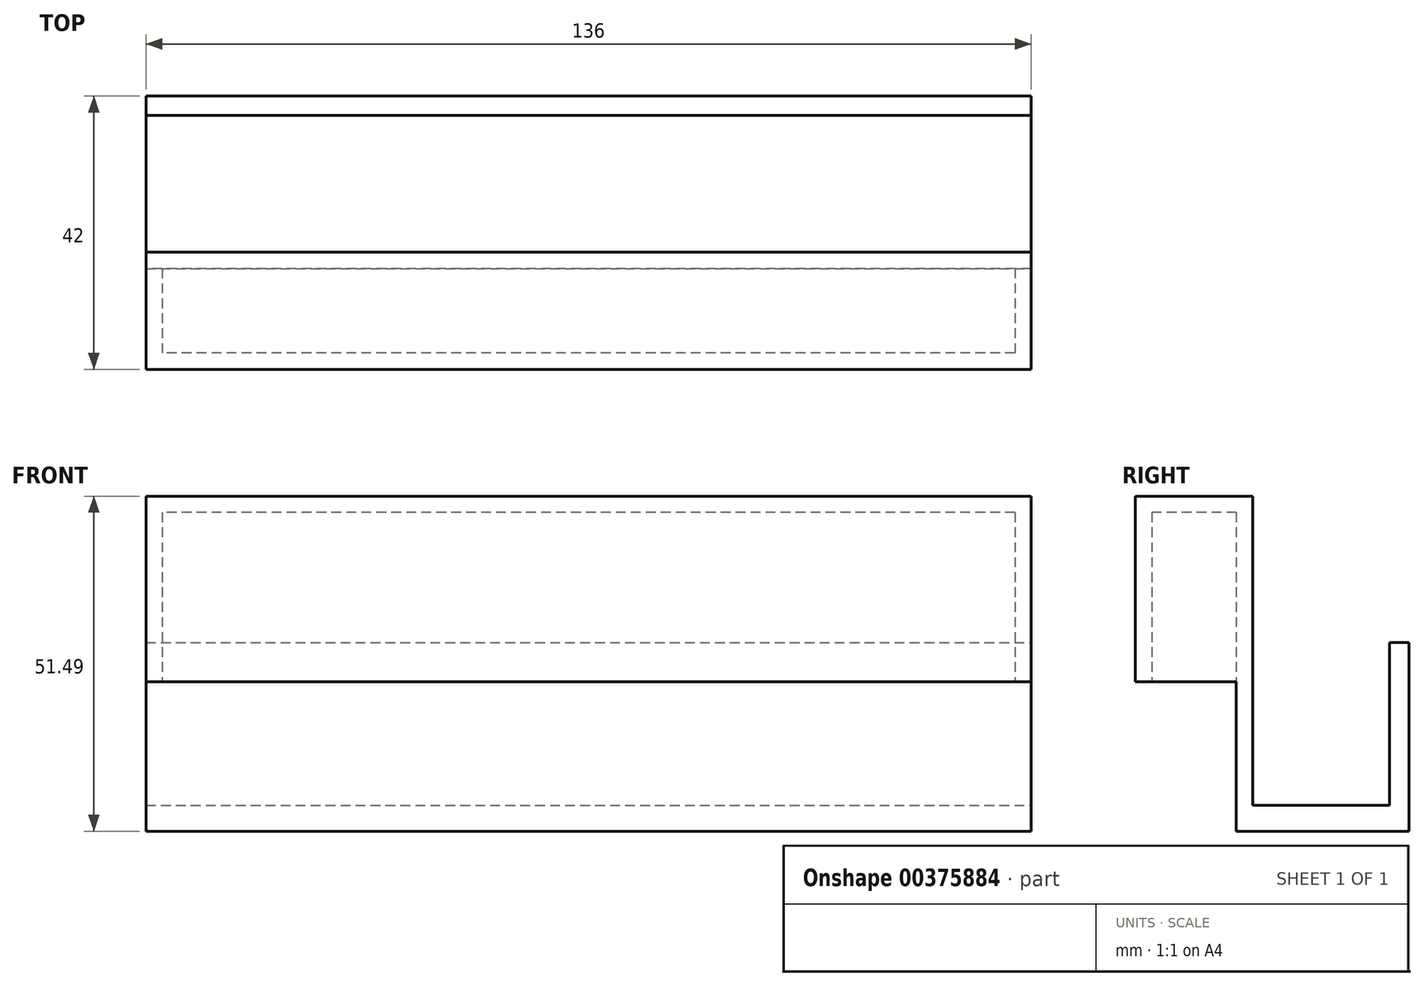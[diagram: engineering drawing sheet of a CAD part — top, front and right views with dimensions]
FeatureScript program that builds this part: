
annotation { "Feature Type Name" : "Feature", "Feature Type Description" : "" }
export const myFeature = defineFeature(function(context is Context, id is Id, definition is map)
    precondition{}
    {
        {
            var Q0;
            Q0=qCreatedBy(makeId("Top.planeOp"),FACE);
            var sketch = newSketch(context, id + "F0", { "sketchPlane" : qUnion([Q0])});
            skLineSegment(sketch, "E0.bottom", {"start": v(65.5, 6.5) * mm, "end": v(-65.5, 6.5) * mm});
            skLineSegment(sketch, "E0.top", {"start": v(65.5, -6.5) * mm, "end": v(-65.5, -6.5) * mm});
            skLineSegment(sketch, "E0.left", {"start": v(65.5, 6.5) * mm, "end": v(65.5, -6.5) * mm});
            skLineSegment(sketch, "E0.right", {"start": v(-65.5, 6.5) * mm, "end": v(-65.5, -6.5) * mm});
            skPoint(sketch, "E0.middle", {"position": v(0, 0) * mm});
            skSolve(sketch);
        }
        {
            var Q0;
            Q0=makeQuery(id+"F0.imprint","IMPRINT",FACE,{"disambiguationData":[TD([[makeQuery(id+"F0.imprint","IMPRINT",EDGE,{"derivedFrom":sQuery(id+"F0.wireOp",EDGE,"E0.bottom")}),1.0]])]});
            extrude(context, id + "F1", {"entities" : qUnion([Q0]), "depth" : 26 * mm});
        }
        {
            var Q0;
            Q0=makeQuery(id+"F1.opExtrude","CAP_FACE",FACE,{"disambiguationData":[OSD([sQuery(id+"F0.wireOp",EDGE,"E0.bottom"),sQuery(id+"F0.wireOp",EDGE,"E0.top"),sQuery(id+"F0.wireOp",EDGE,"E0.left"),sQuery(id+"F0.wireOp",EDGE,"E0.right")])],"isStart":true});
            shell(context, id + "F2", {"entities" : qUnion([Q0]), "thickness" : 2.5 * mm, "oppositeDirection" : true});
        }
        {
            var Q0;
            Q0=makeQuery(id+"F1.opExtrude","SWEPT_FACE",FACE,{"disambiguationData":[OSD([sQuery(id+"F0.wireOp",EDGE,"E0.bottom")])]});
            var sketch = newSketch(context, id + "F3", { "sketchPlane" : qUnion([Q0])});
            skLineSegment(sketch, "E1.bottom", {"start": v(68, 28.5) * mm, "end": v(-68, 28.5) * mm});
            skLineSegment(sketch, "E1.top", {"start": v(68, -23) * mm, "end": v(-68, -23) * mm});
            skLineSegment(sketch, "E1.left", {"start": v(68, 28.5) * mm, "end": v(68, -23) * mm});
            skLineSegment(sketch, "E1.right", {"start": v(-68, 28.5) * mm, "end": v(-68, -23) * mm});
            skSolve(sketch);
        }
        {
            var Q0;
            {var subQ0=sQuery(id+"F3.wireOp",EDGE,"E1.top");Q0=makeQuery(id+"F3.imprint","IMPRINT",FACE,{"disambiguationData":[TD([[makeQuery(id+"F3.imprint","IMPRINT",EDGE,{"derivedFrom":subQ0}),-1.0]])]});}
            extrude(context, id + "F4", {"entities" : qUnion([Q0]), "operationType" : NewBodyOperationType.ADD, "oppositeDirection" : true, "depth" : 2.5 * mm});
        }
        {
            var Q0;
            {var subQ0=sQuery(id+"F0.wireOp",EDGE,"E0.bottom");Q0=makeQuery(id+"F4.boolean.opBoolean","MERGE",FACE,{"derivedFrom":[makeQuery(id+"F1.opExtrude","SWEPT_FACE",FACE,{"disambiguationData":[OSD([subQ0])]}),makeQuery(id+"F4.opExtrude","CAP_FACE",FACE,{"disambiguationData":[OSD([subQ0,sQuery(id+"F3.wireOp",EDGE,"E1.top"),sQuery(id+"F3.wireOp",EDGE,"E1.left"),sQuery(id+"F3.wireOp",EDGE,"E1.right")])],"isStart":true})]});}
            var sketch = newSketch(context, id + "F5", { "sketchPlane" : qUnion([Q0])});
            skLineSegment(sketch, "E2.bottom", {"start": v(68, -23) * mm, "end": v(-68, -23) * mm});
            skLineSegment(sketch, "E2.top", {"start": v(68, -19) * mm, "end": v(-68, -19) * mm});
            skLineSegment(sketch, "E2.left", {"start": v(68, -23) * mm, "end": v(68, -19) * mm});
            skLineSegment(sketch, "E2.right", {"start": v(-68, -23) * mm, "end": v(-68, -19) * mm});
            skSolve(sketch);
        }
        {
            var Q0;
            Q0=makeQuery(id+"F5.imprint","IMPRINT",FACE,{"disambiguationData":[TD([[makeQuery(id+"F5.imprint","IMPRINT",EDGE,{"derivedFrom":sQuery(id+"F5.wireOp",EDGE,"E2.bottom")}),-1.0]])]});
            extrude(context, id + "F6", {"entities" : qUnion([Q0]), "operationType" : NewBodyOperationType.ADD, "depth" : 24 * mm});
        }
        {
            var Q0;
            Q0=makeQuery(id+"F6.opExtrude","SWEPT_FACE",FACE,{"disambiguationData":[OSD([sQuery(id+"F5.wireOp",EDGE,"E2.top")])]});
            var sketch = newSketch(context, id + "F7", { "sketchPlane" : qUnion([Q0])});
            skLineSegment(sketch, "E3.bottom", {"start": v(-68, 33) * mm, "end": v(68, 33) * mm});
            skLineSegment(sketch, "E3.top", {"start": v(-68, 30) * mm, "end": v(68, 30) * mm});
            skLineSegment(sketch, "E3.left", {"start": v(-68, 33) * mm, "end": v(-68, 30) * mm});
            skLineSegment(sketch, "E3.right", {"start": v(68, 33) * mm, "end": v(68, 30) * mm});
            skSolve(sketch);
        }
        {
            var Q0;
            Q0=makeQuery(id+"F7.imprint","IMPRINT",FACE,{"disambiguationData":[TD([[makeQuery(id+"F7.imprint","IMPRINT",EDGE,{"derivedFrom":sQuery(id+"F7.wireOp",EDGE,"E3.bottom")}),-1.0]])]});
            extrude(context, id + "F8", {"entities" : qUnion([Q0]), "operationType" : NewBodyOperationType.ADD, "depth" : 25 * mm});
        }
    });
